# Revit family: highbay_21_51hla1d24mlb
name_source: partatom
category: Lighting Fixtures
units: mm (PartAtom-declared; Revit-internal decimal feet)

## family parameters
Cut with Voids When Loaded = No
Host = Face
Light Source = No
Part Type = Normal
Room Calculation Point = No
Round Connector Dimension = Use Diameter
Shared = No

## types (1)
- --- (1 x LED, 26940 lm, 171.1 W, 4000K)
    Apparent Load = 342 VA
    CIE Flux Codes = 88 95 99 100 99
    Color Rendering = 80
    Color Temperature = 4000K
    Default Elevation = 1800 mm
    Description = Highbay 21, LED high bay luminaire, end cap, primary light control with lens, of PMMA, light emission: direct distribution, primary light characteristic: symmetric, installation type: recessed, for 2x 2x LED, rated luminous flux: 26.940lm, luminous efficacy: 157lm/W, light colour: 840, colour temperature: 4000K, control gear: ECG DALI, with system connector, mains connection: 230..240V, AC, 50/60Hz, rated input power: 171W, LED unit, of diecast aluminium, unplated, bead blasted, silver, for tool-free mounting of luminaire to Licross® trunking rail, length: 1.500mm, width: 500mm, height: 65mm, housing, of diecast aluminium, uncoated, bead blasted, silver, fixing on rail side, of aluminium, anodised, metallic grey, end cap, of PC, grey, protection rating (complete): IP64, insulation class (complete): insulation class I (protective earthing), certification: CE, UKCA, protection symbol: D, impact resistance: IK08 with glass or PC cover, permissible operating ambient temperature: -35..+40°C, corresponds to IFS (International Featured Standards) requirements for safety and quality in the food industry, reducing of maximum allowable ambient temperature of 5°C with ceiling mounting, packaging unit: 1 piece
    Height = 105 mm
    Lamp = 1 x LED
    Lamp Light Flux = 26940 lm
    Lamp Power = 171.1 W
    Lamp count = 1
    Length = 1500 mm
    Luminous efficacy = 157 lm/W
    Manufacturer = Siteco
    ModVariant = No
    Model = 51HLA1D24MLB
    Mounting Place = Ceiling
    Mounting Type = Pendant
    Number of Poles = 1
    OnlyDefault = Yes
    Power Factor = 1
    Product Name = Highbay 21
    Product group = LED high bay luminaire
    ProductGroupID = 903
    Protection Class = Protection class I
    Protection Degree = IP 64
    RLX_Detail_Level = 1
    RLX_Emergency_Light_Flux = 0 lm
    RLX_Emergency_Type = 0
    RLX_Emergency_Type_DB = No
    RlxData = <blob elided: 46149 chars, md5=39d59b70>
    Socket = socket
    Standby Power = 0 W
    System Light Flux = 53880 lm
    System Power = 342 W
    Type Comments = factory setting: luminous flux: 100 % | dim-lin: 254 | 490 mA
    Type Image = l_1004707.jpg
    URL = http://relux.com
    VarID = @adj_141869
    Voltage = 0 V
    Weight = 0.00 kg
    Width = 500 mm

## geometry (parser evidence)
native form markers: Sweep x16
no freeform markers — native parametric forms only
